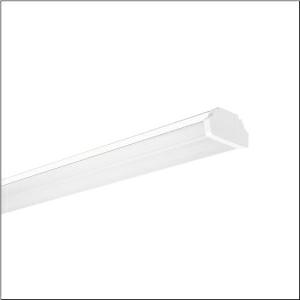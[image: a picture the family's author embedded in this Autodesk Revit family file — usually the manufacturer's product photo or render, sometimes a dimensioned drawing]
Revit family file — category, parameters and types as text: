
# Revit family: dus_r__31_mo_53bd812d2v4085_2fe7
name_source: partatom
category: Lighting Fixtures
units: mm (PartAtom-declared; Revit-internal decimal feet)

## family parameters
Cut with Voids When Loaded = No
Host = Face
Light Source = No
Part Type = Normal
Room Calculation Point = No
Round Connector Dimension = Use Diameter
Shared = No

## types (1)
- --- (1 x LED, 8930 lm, 61.8 W, 4000K)
    Apparent Load = 62 VA
    CIE Flux Codes = 47 80 95 92 100
    Color Rendering = 80
    Color Temperature = 4000K
    Default Elevation = 1800 mm
    Description = DUS® 31 MO, luminaire insert, of sheet steel, coil coated, white, length: 1.535mm, width: 81mm, height: 90mm, 5x system unit, system units: 307mm, LED rated luminous flux: 8.930lm, light colour: 840, control gear: DALI 2, control gear: ECG DALI, with plug, 5-pole, with phase selection, mains connection: 220..240V, AC, 50/60Hz, rated input power: 62W, through-wiring accessed according to module size, primary optical cover: cover, of PMMA, light emission: direct distribution, primary light characteristic: symmetric, protection rating (complete): IP20, protection rating (LED compartment): IP50, insulation class (complete): insulation class I (protective earthing), certification: CE, ENEC, VDE, UKCA, impact resistance: IK03, permissible ambient temperature for indoor applications: -25..+30°C, corresponds to IFS (International Featured Standards) requirements for safety and quality in the food industry, reducing of maximum allowable ambient temperature of 5°C with ceiling mounting, packaging unit: 1 piece
    Height = 95 mm
    Lamp = 1 x LED
    Lamp Light Flux = 8930 lm
    Lamp Power = 61.8 W
    Lamp count = 1
    Length = 1535 mm
    Luminous efficacy = 145 lm/W
    Manufacturer = Siteco
    ModVariant = No
    Model = 53BD812D2V4085
    Mounting Place = Ceiling
    Mounting Type = Pendant
    Number of Poles = 1
    OnlyDefault = Yes
    Power Factor = 1
    Product Name = DUS® 31 MO
    Product group = luminaire insert
    ProductGroupID = 901
    Protection Class = Protection class I
    Protection Degree = IP 20
    RLX_Detail_Level = 1
    RLX_Emergency_Light_Flux = 0 lm
    RLX_Emergency_Type = 0
    RLX_Emergency_Type_DB = No
    RlxData = <blob elided: 42117 chars, md5=bc3df98b>
    Socket = socket
    Standby Power = 0 W
    System Light Flux = 8930 lm
    System Power = 62 W
    Type Comments = factory setting: luminous flux: 100 % | dim-lin: 254 | 500 mA
    Type Image = l_1003451.jpg
    URL = http://relux.com
    VarID = @adj_130963
    Voltage = 0 V
    Weight = 0.00 kg
    Width = 81 mm

## geometry (parser evidence)
native form markers: Blend x4, Sweep x13
no freeform markers — native parametric forms only
